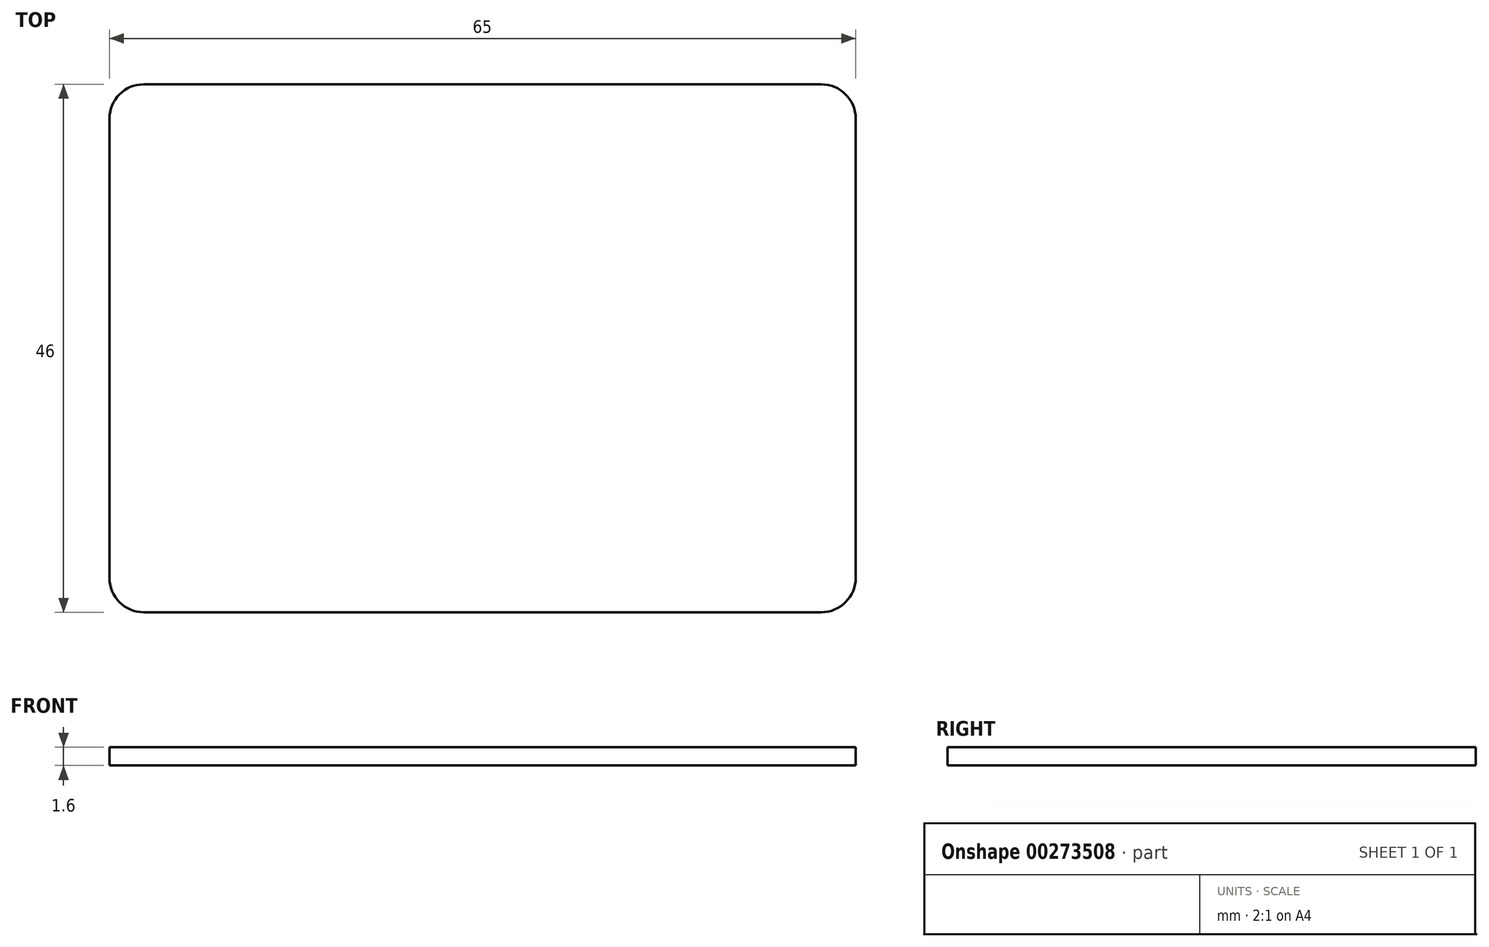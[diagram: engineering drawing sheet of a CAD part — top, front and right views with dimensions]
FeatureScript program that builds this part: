
annotation { "Feature Type Name" : "Feature", "Feature Type Description" : "" }
export const myFeature = defineFeature(function(context is Context, id is Id, definition is map)
    precondition{}
    {
        {
            var Q0;
            Q0=qCreatedBy(makeId("Top.planeOp"),FACE);
            var sketch = newSketch(context, id + "F0", { "sketchPlane" : qUnion([Q0])});
            skLineSegment(sketch, "E0.bottom", {"start": v(32.5, -23) * mm, "end": v(-32.5, -23) * mm});
            skLineSegment(sketch, "E0.top", {"start": v(32.5, 23) * mm, "end": v(-32.5, 23) * mm});
            skLineSegment(sketch, "E0.left", {"start": v(32.5, -23) * mm, "end": v(32.5, 23) * mm});
            skLineSegment(sketch, "E0.right", {"start": v(-32.5, -23) * mm, "end": v(-32.5, 23) * mm});
            skPoint(sketch, "E0.middle", {"position": v(0, 0) * mm});
            skSolve(sketch);
        }
        {
            var Q0;
            Q0 = qSketchRegion(id + "F0", true);
            extrude(context, id + "F1", {"entities" : qUnion([Q0]), "flatOperationType" : FlatOperationType.REMOVE, "depth" : 1.6 * mm, "offsetDistance" : 25 * mm, "domain" : OperationDomain.MODEL});
        }
        {
            var Q0;
            Q0=makeQuery(id+"F1.opExtrude","SWEPT_EDGE",EDGE,{"disambiguationData":[OSD([sQuery(id+"F0.wireOp",EDGE,"E0.top"),sQuery(id+"F0.wireOp",EDGE,"E0.left")])]});
            var Q1;
            Q1=makeQuery(id+"F1.opExtrude","SWEPT_EDGE",EDGE,{"disambiguationData":[OSD([sQuery(id+"F0.wireOp",EDGE,"E0.bottom"),sQuery(id+"F0.wireOp",EDGE,"E0.left")])]});
            var Q2;
            Q2=makeQuery(id+"F1.opExtrude","SWEPT_EDGE",EDGE,{"disambiguationData":[OSD([sQuery(id+"F0.wireOp",EDGE,"E0.bottom"),sQuery(id+"F0.wireOp",EDGE,"E0.right")])]});
            var Q3;
            Q3=makeQuery(id+"F1.opExtrude","SWEPT_EDGE",EDGE,{"disambiguationData":[OSD([sQuery(id+"F0.wireOp",EDGE,"E0.top"),sQuery(id+"F0.wireOp",EDGE,"E0.right")])]});
            fillet(context, id + "F2", {"entities" : qUnion([Q0, Q1, Q2, Q3]), "tangentPropagation" : true, "radius" : 3 * mm, "defaultsChanged" : false, "vertexSettings" : [], "allowEdgeOverflow" : false});
        }
    });
